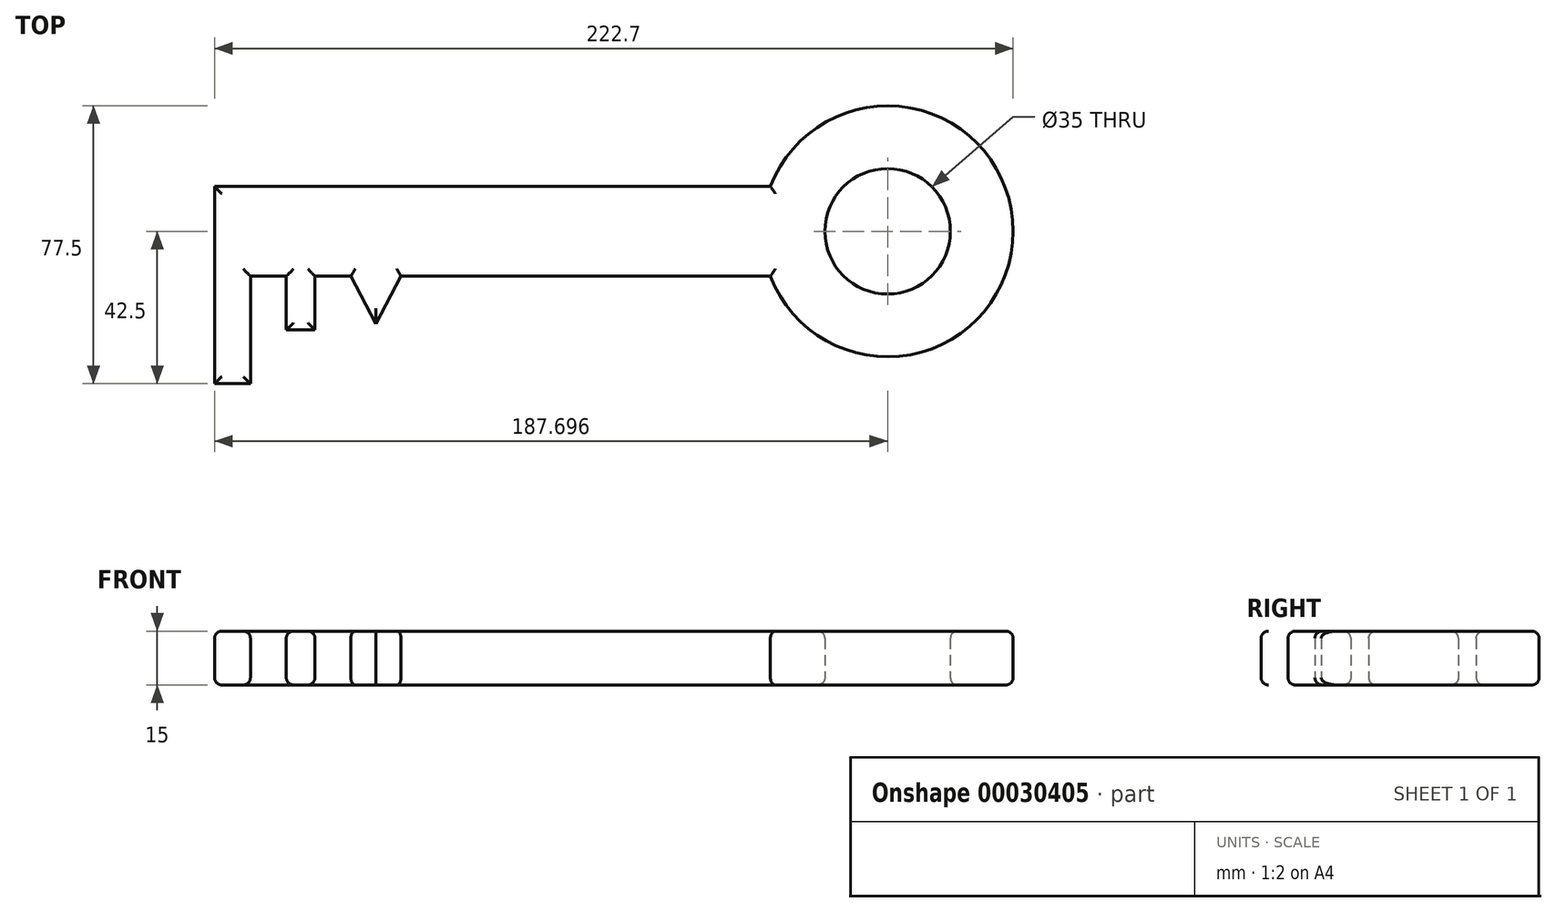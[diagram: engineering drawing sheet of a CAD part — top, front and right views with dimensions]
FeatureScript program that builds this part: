
annotation { "Feature Type Name" : "Feature", "Feature Type Description" : "" }
export const myFeature = defineFeature(function(context is Context, id is Id, definition is map)
    precondition{}
    {
        {
            var Q0;
            Q0=qCreatedBy(makeId("Top.planeOp"),FACE);
            var sketch = newSketch(context, id + "F0", { "sketchPlane" : qUnion([Q0])});
            skLineSegment(sketch, "E0.bottom", {"start": v(11, 23.49) * mm, "end": v(-144, 23.49) * mm});
            skLineSegment(sketch, "E0.top", {"start": v(11, -1.51) * mm, "end": v(-92, -1.51) * mm});
            skLineSegment(sketch, "E0.right", {"start": v(-144, 23.49) * mm, "end": v(-144, -1.51) * mm});
            skLineSegment(sketch, "E1.top", {"start": v(-144, -31.51) * mm, "end": v(-134, -31.51) * mm});
            skLineSegment(sketch, "E1.left", {"start": v(-144, -1.51) * mm, "end": v(-144, -31.51) * mm});
            skLineSegment(sketch, "E1.right", {"start": v(-134, -1.51) * mm, "end": v(-134, -31.51) * mm});
            skLineSegment(sketch, "E2.top", {"start": v(-124, -16.51) * mm, "end": v(-116, -16.51) * mm});
            skLineSegment(sketch, "E2.left", {"start": v(-124, -1.51) * mm, "end": v(-124, -16.51) * mm});
            skLineSegment(sketch, "E2.right", {"start": v(-116, -1.51) * mm, "end": v(-116, -16.51) * mm});
            skLineSegment(sketch, "E3", {"start": v(-106, -1.51) * mm, "end": v(-99, -14.78) * mm});
            skLineSegment(sketch, "E4", {"start": v(-99, -14.78) * mm, "end": v(-92, -1.51) * mm});
            skArc(sketch, "E5", {"start": v(11, -1.51) * mm, "mid": v(78.69, 10.99) * mm, "end": v(11, 23.49) * mm});
            skCircle(sketch, "E6", {"center": v(43.69, 10.99) * mm, "radius": 17.5 * mm});
            skLineSegment(sketch, "E7", {"start": v(43.69, 10.99) * mm, "end": v(-144, 10.99) * mm, "construction": true});
            skLineSegment(sketch, "E8.trimOffspring", {"start": v(-124, -1.51) * mm, "end": v(-134, -1.51) * mm});
            skLineSegment(sketch, "E9.trimOffspring", {"start": v(-106, -1.51) * mm, "end": v(-116, -1.51) * mm});
            skSolve(sketch);
        }
        {
            var Q0;
            Q0 = qSketchRegion(id + "F0", true);
            extrude(context, id + "F1", {"entities" : qUnion([Q0]), "depth" : 15 * mm});
        }
        {
            var Q0;
            Q0=makeQuery(id+"F1.opExtrude","CAP_EDGE",EDGE,{"disambiguationData":[OSD([sQuery(id+"F0.wireOp",EDGE,"E5")])],"isStart":true});
            var Q1;
            Q1=makeQuery(id+"F1.opExtrude","CAP_EDGE",EDGE,{"disambiguationData":[OSD([sQuery(id+"F0.wireOp",EDGE,"E0.bottom")])],"isStart":true});
            var Q2;
            Q2=makeQuery(id+"F1.opExtrude","CAP_EDGE",EDGE,{"disambiguationData":[OSD([sQuery(id+"F0.wireOp",EDGE,"E0.top")])],"isStart":true});
            var Q3;
            Q3=makeQuery(id+"F1.opExtrude","CAP_EDGE",EDGE,{"disambiguationData":[OSD([sQuery(id+"F0.wireOp",EDGE,"E4")])],"isStart":true});
            var Q4;
            Q4=makeQuery(id+"F1.opExtrude","CAP_EDGE",EDGE,{"disambiguationData":[OSD([sQuery(id+"F0.wireOp",EDGE,"E3")])],"isStart":true});
            var Q5;
            Q5=makeQuery(id+"F1.opExtrude","CAP_EDGE",EDGE,{"disambiguationData":[OSD([sQuery(id+"F0.wireOp",EDGE,"E2.right")])],"isStart":true});
            var Q6;
            Q6=makeQuery(id+"F1.opExtrude","CAP_EDGE",EDGE,{"disambiguationData":[OSD([sQuery(id+"F0.wireOp",EDGE,"E2.left")])],"isStart":true});
            var Q7;
            Q7=makeQuery(id+"F1.opExtrude","CAP_EDGE",EDGE,{"disambiguationData":[OSD([sQuery(id+"F0.wireOp",EDGE,"E1.right")])],"isStart":true});
            var Q8;
            Q8=makeQuery(id+"F1.opExtrude","CAP_EDGE",EDGE,{"disambiguationData":[OSD([sQuery(id+"F0.wireOp",EDGE,"E0.right"),sQuery(id+"F0.wireOp",EDGE,"E1.left")])],"isStart":true});
            var Q9;
            Q9=makeQuery(id+"F1.opExtrude","CAP_EDGE",EDGE,{"disambiguationData":[OSD([sQuery(id+"F0.wireOp",EDGE,"E6")])],"isStart":true});
            var Q10;
            Q10=makeQuery(id+"F1.opExtrude","CAP_EDGE",EDGE,{"disambiguationData":[OSD([sQuery(id+"F0.wireOp",EDGE,"E9.trimOffspring")])],"isStart":true});
            var Q11;
            Q11=makeQuery(id+"F1.opExtrude","CAP_EDGE",EDGE,{"disambiguationData":[OSD([sQuery(id+"F0.wireOp",EDGE,"E8.trimOffspring")])],"isStart":true});
            var Q12;
            Q12=makeQuery(id+"F1.opExtrude","CAP_EDGE",EDGE,{"disambiguationData":[OSD([sQuery(id+"F0.wireOp",EDGE,"E2.top")])],"isStart":true});
            var Q13;
            Q13=makeQuery(id+"F1.opExtrude","CAP_EDGE",EDGE,{"disambiguationData":[OSD([sQuery(id+"F0.wireOp",EDGE,"E1.top")])],"isStart":true});
            fillet(context, id + "F2", {"entities" : qUnion([Q0, Q1, Q2, Q3, Q4, Q5, Q6, Q7, Q8, Q9, Q10, Q11, Q12, Q13]), "radius" : 2 * mm, "tangentPropagation" : true, "allowEdgeOverflow" : false});
        }
        {
            var Q0;
            Q0=makeQuery(id+"F1.opExtrude","CAP_EDGE",EDGE,{"disambiguationData":[OSD([sQuery(id+"F0.wireOp",EDGE,"E0.bottom")])],"isStart":false});
            var Q1;
            Q1=makeQuery(id+"F1.opExtrude","CAP_EDGE",EDGE,{"disambiguationData":[OSD([sQuery(id+"F0.wireOp",EDGE,"E0.right"),sQuery(id+"F0.wireOp",EDGE,"E1.left")])],"isStart":false});
            var Q2;
            Q2=makeQuery(id+"F1.opExtrude","CAP_EDGE",EDGE,{"disambiguationData":[OSD([sQuery(id+"F0.wireOp",EDGE,"E1.top")])],"isStart":false});
            var Q3;
            Q3=makeQuery(id+"F1.opExtrude","CAP_EDGE",EDGE,{"disambiguationData":[OSD([sQuery(id+"F0.wireOp",EDGE,"E1.right")])],"isStart":false});
            var Q4;
            Q4=makeQuery(id+"F1.opExtrude","CAP_EDGE",EDGE,{"disambiguationData":[OSD([sQuery(id+"F0.wireOp",EDGE,"E8.trimOffspring")])],"isStart":false});
            var Q5;
            Q5=makeQuery(id+"F1.opExtrude","CAP_EDGE",EDGE,{"disambiguationData":[OSD([sQuery(id+"F0.wireOp",EDGE,"E2.left")])],"isStart":false});
            var Q6;
            Q6=makeQuery(id+"F1.opExtrude","CAP_EDGE",EDGE,{"disambiguationData":[OSD([sQuery(id+"F0.wireOp",EDGE,"E2.top")])],"isStart":false});
            var Q7;
            Q7=makeQuery(id+"F1.opExtrude","CAP_EDGE",EDGE,{"disambiguationData":[OSD([sQuery(id+"F0.wireOp",EDGE,"E2.right")])],"isStart":false});
            var Q8;
            Q8=makeQuery(id+"F1.opExtrude","CAP_EDGE",EDGE,{"disambiguationData":[OSD([sQuery(id+"F0.wireOp",EDGE,"E9.trimOffspring")])],"isStart":false});
            var Q9;
            Q9=makeQuery(id+"F1.opExtrude","CAP_EDGE",EDGE,{"disambiguationData":[OSD([sQuery(id+"F0.wireOp",EDGE,"E3")])],"isStart":false});
            var Q10;
            Q10=makeQuery(id+"F1.opExtrude","CAP_EDGE",EDGE,{"disambiguationData":[OSD([sQuery(id+"F0.wireOp",EDGE,"E4")])],"isStart":false});
            var Q11;
            Q11=makeQuery(id+"F1.opExtrude","CAP_EDGE",EDGE,{"disambiguationData":[OSD([sQuery(id+"F0.wireOp",EDGE,"E0.top")])],"isStart":false});
            var Q12;
            Q12=makeQuery(id+"F1.opExtrude","CAP_EDGE",EDGE,{"disambiguationData":[OSD([sQuery(id+"F0.wireOp",EDGE,"E5")])],"isStart":false});
            var Q13;
            Q13=makeQuery(id+"F1.opExtrude","CAP_EDGE",EDGE,{"disambiguationData":[OSD([sQuery(id+"F0.wireOp",EDGE,"E6")])],"isStart":false});
            fillet(context, id + "F3", {"entities" : qUnion([Q0, Q1, Q2, Q3, Q4, Q5, Q6, Q7, Q8, Q9, Q10, Q11, Q12, Q13]), "radius" : 2 * mm, "tangentPropagation" : true, "allowEdgeOverflow" : false});
        }
    });
